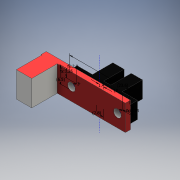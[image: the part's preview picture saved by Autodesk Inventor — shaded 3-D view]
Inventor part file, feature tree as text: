
AUTODESK INVENTOR PART (.ipt)
format: ipt  version: 2016 SP1 (Build 200210100, 210)  size: 160,768 bytes
history: native  units: mm
features: extrude x4, sketch x3
ambient origin geometry x8: Origin, YZ Plane, XZ Plane, XY Plane, X Axis, Y Axis, Z Axis, Center Point
bodies: Solid1 (feature_tree)
feature tree (7):
  extrude  "Extrusion1"  Depth=6.0mm
  extrude  "Extrusion2"  Depth=4.4mm
  extrude  "Extrusion3"  Depth=4.4mm
  extrude  "Extrusion4"  Depth=6.0mm
  sketch  "Sketch1"  dims[d0=3.0mm d1=6.0mm]
  sketch  "Sketch3"  dims[d2=8.0mm d3=4.4mm]
  sketch  "Sketch4"  dims[d4=2.8mm d5=4.4mm d6=6.0mm d7=1.4mm d8=0.0mm d9=6.5mm d10=0.0mm d11=3.0mm d12=3.0mm d13=18.0mm d14=23.6mm d15=2.8mm d16=6.5mm d17=3.25mm d18=3.25mm d19=6.5mm d20=0.0mm d21=10.0mm d22=33.0mm d23=0.3mm d24=6.5mm d25=1.75mm d26=2.0mm d27=0.0mm d28=10.0mm d29=6.0mm d30=0.0mm d31=0.3mm d32=10.0mm d33=0.0mm d34=2.8mm d35=1.4mm]
